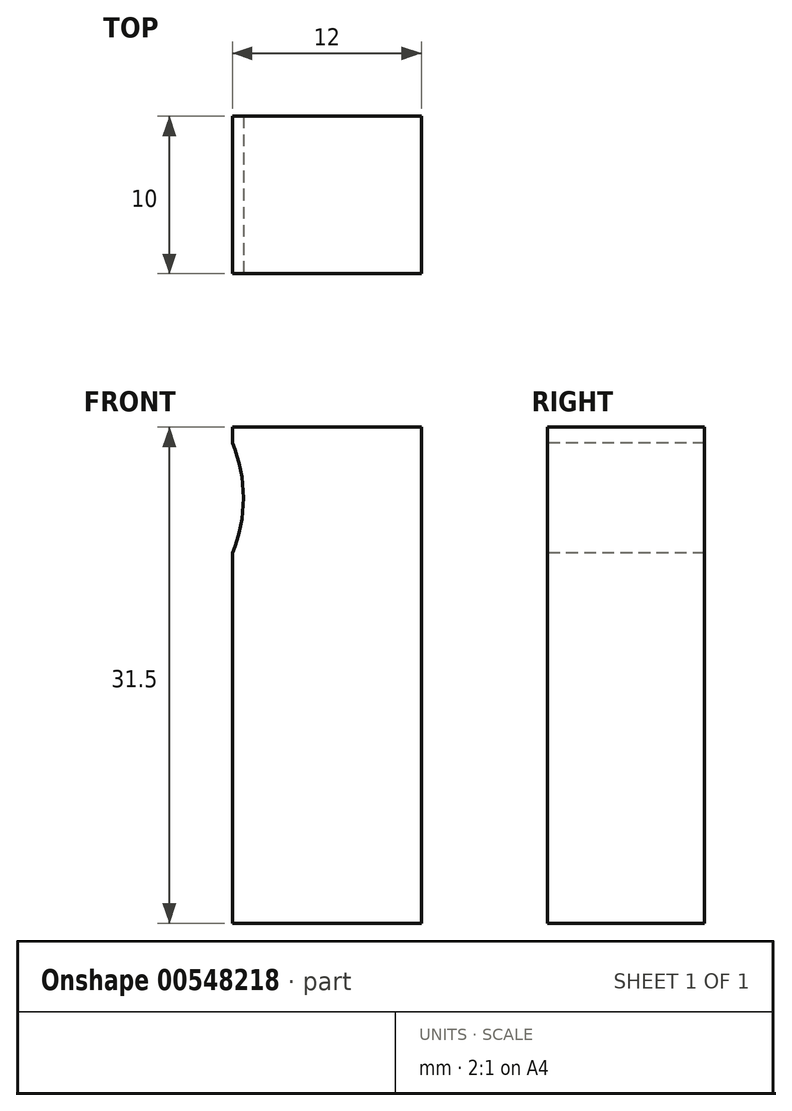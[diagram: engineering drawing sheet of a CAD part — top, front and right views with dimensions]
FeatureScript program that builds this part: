
annotation { "Feature Type Name" : "Feature", "Feature Type Description" : "" }
export const myFeature = defineFeature(function(context is Context, id is Id, definition is map)
    precondition{}
    {
        {
            var Q0;
            Q0=qCreatedBy(makeId("Front.planeOp"),FACE);
            var sketch = newSketch(context, id + "F0", { "sketchPlane" : qUnion([Q0])});
            skLineSegment(sketch, "E0.bottom", {"start": v(0, 0) * mm, "end": v(12, 0) * mm});
            skLineSegment(sketch, "E0.top", {"start": v(0, 31.5) * mm, "end": v(12, 31.5) * mm});
            skLineSegment(sketch, "E0.left", {"start": v(0, 0) * mm, "end": v(0, 31.5) * mm});
            skLineSegment(sketch, "E0.right", {"start": v(12, 0) * mm, "end": v(12, 31.5) * mm});
            skSolve(sketch);
        }
        {
            var Q0;
            Q0 = qSketchRegion(id + "F0", true);
            extrude(context, id + "F1", {"entities" : qUnion([Q0]), "depth" : 10 * mm, "offsetDistance" : 25 * mm});
        }
        {
            var Q0;
            Q0=makeQuery(id+"F1.opExtrude","CAP_FACE",FACE,{"disambiguationData":[OSD([sQuery(id+"F0.wireOp",EDGE,"E0.bottom"),sQuery(id+"F0.wireOp",EDGE,"E0.top"),sQuery(id+"F0.wireOp",EDGE,"E0.left"),sQuery(id+"F0.wireOp",EDGE,"E0.right")])],"isStart":false});
            var sketch = newSketch(context, id + "F2", { "sketchPlane" : qUnion([Q0])});
            skArc(sketch, "E1", {"start": v(0, 23.5) * mm, "mid": v(0.7, 27) * mm, "end": v(0, 30.5) * mm});
            skSolve(sketch);
        }
        {
            var Q0;
            Q0 = qSketchRegion(id + "F2", true);
            var Q1;
            {var subQ0=sQuery(id+"F2.wireOp",EDGE,"Q4mulkz5-gN2z-0PnF-tPHA-FkKEU6auD8E9");Q1=makeQuery(id+"F2.imprint","IMPRINT",FACE,{"disambiguationData":[TD([[makeQuery(id+"F2.imprint","IMPRINT",EDGE,{"derivedFrom":subQ0}),1.0]])]});}
            var Q2;
            {var subQ0=sQuery(id+"F2.wireOp",EDGE,"E1");Q2=makeQuery(id+"F2.imprint","IMPRINT",FACE,{"disambiguationData":[TD([[makeQuery(id+"F2.imprint","IMPRINT",EDGE,{"derivedFrom":subQ0}),1.0]])]});}
            extrude(context, id + "F3", {"entities" : qUnion([Q0, Q1, Q2]), "operationType" : NewBodyOperationType.REMOVE, "endBound" : BoundingType.THROUGH_ALL, "oppositeDirection" : true, "depth" : 25 * mm, "offsetDistance" : 25 * mm});
        }
    });
